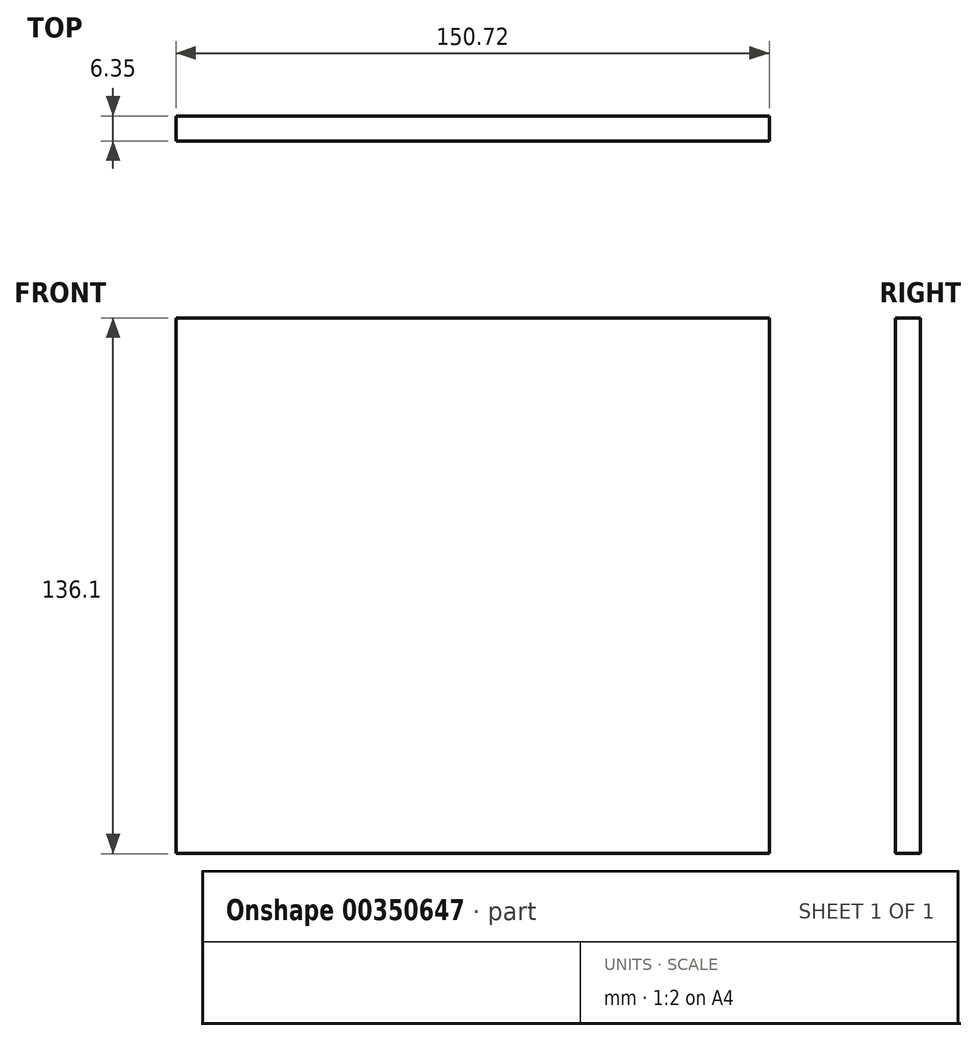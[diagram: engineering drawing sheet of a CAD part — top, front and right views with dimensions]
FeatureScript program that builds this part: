
annotation { "Feature Type Name" : "Feature", "Feature Type Description" : "" }
export const myFeature = defineFeature(function(context is Context, id is Id, definition is map)
    precondition{}
    {
        {
            var Q0;
            Q0=qCreatedBy(makeId("Front.planeOp"),FACE);
            var sketch = newSketch(context, id + "F0", { "sketchPlane" : qUnion([Q0])});
            skLineSegment(sketch, "E0.bottom", {"start": v(-74.85, 67.84) * mm, "end": v(75.87, 67.84) * mm});
            skLineSegment(sketch, "E0.top", {"start": v(-74.85, -68.26) * mm, "end": v(75.87, -68.26) * mm});
            skLineSegment(sketch, "E0.left", {"start": v(-74.85, 67.84) * mm, "end": v(-74.85, -68.26) * mm});
            skLineSegment(sketch, "E0.right", {"start": v(75.87, 67.84) * mm, "end": v(75.87, -68.26) * mm});
            skSolve(sketch);
        }
        {
            var Q0;
            Q0 = qSketchRegion(id + "F0", true);
            extrude(context, id + "F1", {"entities" : qUnion([Q0]), "depth" : 6.35 * mm});
        }
    });
